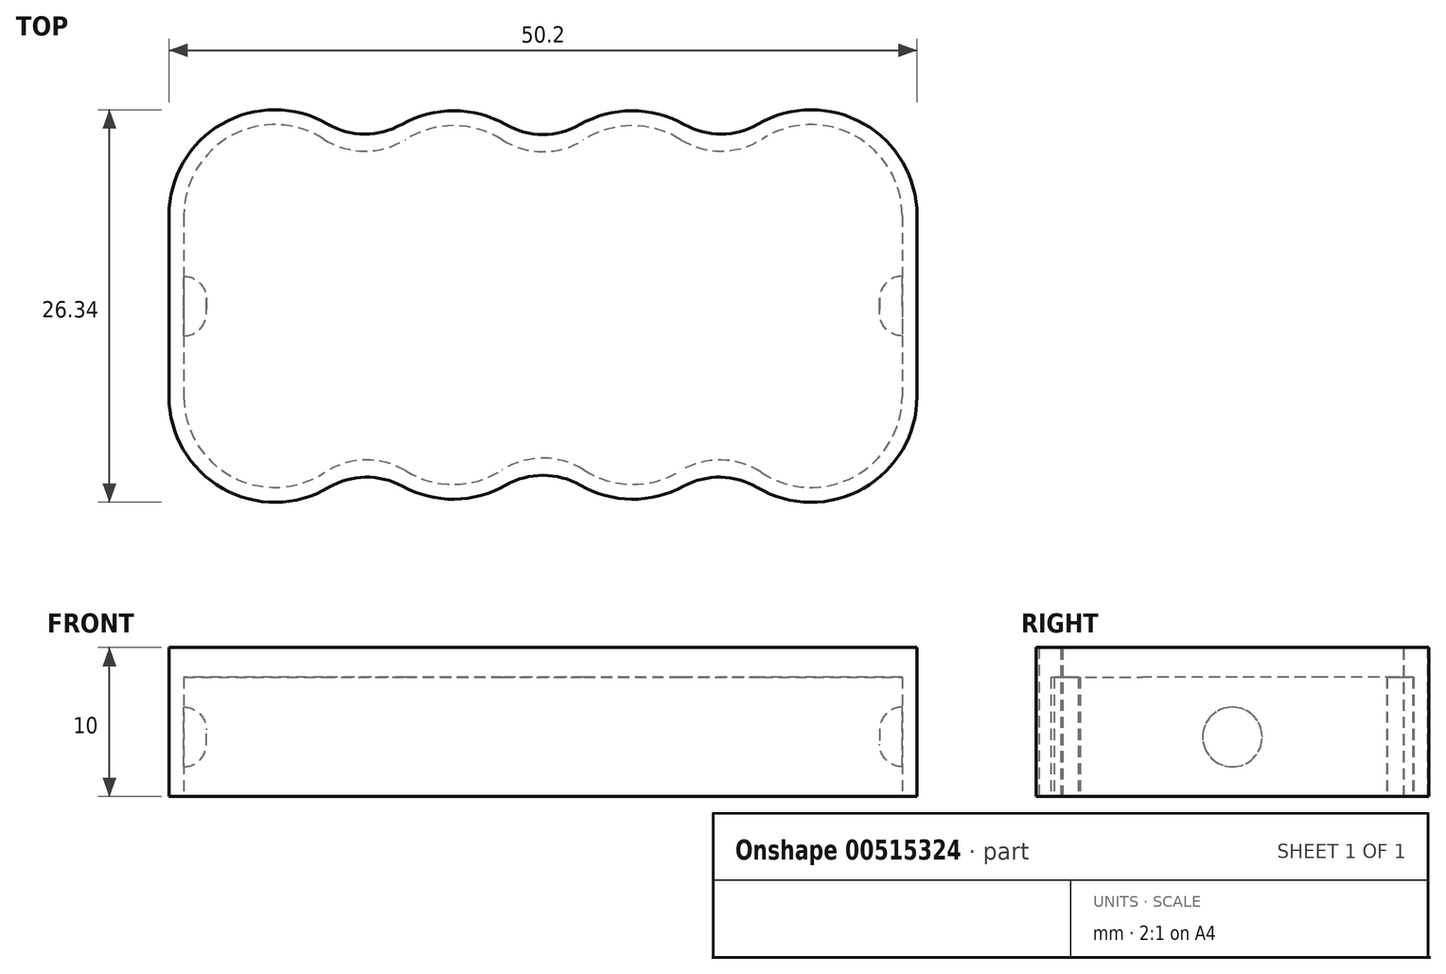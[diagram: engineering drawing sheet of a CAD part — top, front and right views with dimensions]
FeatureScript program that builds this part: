
annotation { "Feature Type Name" : "Feature", "Feature Type Description" : "" }
export const myFeature = defineFeature(function(context is Context, id is Id, definition is map)
    precondition{}
    {
        {
            var Q0;
            Q0=qCreatedBy(makeId("Top.planeOp"),FACE);
            var sketch = newSketch(context, id + "F0", { "sketchPlane" : qUnion([Q0])});
            skArc(sketch, "E0", {"start": v(-12, 7.13) * mm, "mid": v(-18.53, 12.15) * mm, "end": v(-24.1, 6.07) * mm});
            skArc(sketch, "E1", {"start": v(0, 7.1) * mm, "mid": v(-5.98, 12.1) * mm, "end": v(-12, 7.13) * mm});
            skArc(sketch, "E2.MirrorCS", {"start": v(0, -6.81) * mm, "mid": v(-5.86, -11.97) * mm, "end": v(-12, -7.13) * mm});
            skArc(sketch, "E3.MirrorCS", {"start": v(-12, -7.13) * mm, "mid": v(-18.53, -12.15) * mm, "end": v(-24.1, -6.07) * mm});
            skArc(sketch, "E4.MirrorCS", {"start": v(0, -6.81) * mm, "mid": v(5.86, -11.97) * mm, "end": v(12, -7.13) * mm});
            skArc(sketch, "E5.MirrorCS", {"start": v(12, 7.13) * mm, "mid": v(18.53, 12.15) * mm, "end": v(24.1, 6.07) * mm});
            skArc(sketch, "E6.MirrorCS", {"start": v(12, -7.13) * mm, "mid": v(18.53, -12.15) * mm, "end": v(24.1, -6.07) * mm});
            skArc(sketch, "E7.MirrorCS", {"start": v(0, 7.1) * mm, "mid": v(5.98, 12.1) * mm, "end": v(12, 7.13) * mm});
            skCircle(sketch, "E8", {"center": v(-12, 0) * mm, "radius": 2 * mm});
            skCircle(sketch, "E9", {"center": v(0, 0) * mm, "radius": 2 * mm});
            skCircle(sketch, "E10", {"center": v(12, 0) * mm, "radius": 2 * mm});
            skLineSegment(sketch, "E11", {"start": v(-24.1, 6.07) * mm, "end": v(-24.1, -6.07) * mm});
            skLineSegment(sketch, "E12", {"start": v(24.1, 6.07) * mm, "end": v(24.1, -6.07) * mm});
            skArc(sketch, "E13.0", {"start": v(-11.98, 9.83) * mm, "mid": v(-19.96, 12.9) * mm, "end": v(-25.1, 6.07) * mm});
            skArc(sketch, "E14.0", {"start": v(0, 9.8) * mm, "mid": v(-5.98, 13.1) * mm, "end": v(-11.98, 9.83) * mm});
            skArc(sketch, "E15.0", {"start": v(0, 9.8) * mm, "mid": v(5.98, 13.1) * mm, "end": v(11.98, 9.83) * mm});
            skArc(sketch, "E16.0", {"start": v(11.98, 9.83) * mm, "mid": v(19.96, 12.9) * mm, "end": v(25.1, 6.07) * mm});
            skLineSegment(sketch, "E17.0", {"start": v(25.1, 6.07) * mm, "end": v(25.1, -6.18) * mm});
            skArc(sketch, "E18.0", {"start": v(11.95, -9.78) * mm, "mid": v(19.93, -12.9) * mm, "end": v(25.1, -6.07) * mm});
            skArc(sketch, "E19.0", {"start": v(0, -9.62) * mm, "mid": v(5.93, -12.97) * mm, "end": v(11.95, -9.78) * mm});
            skArc(sketch, "E20.0", {"start": v(0, -9.62) * mm, "mid": v(-5.93, -12.97) * mm, "end": v(-11.95, -9.78) * mm});
            skArc(sketch, "E21.0", {"start": v(-11.95, -9.78) * mm, "mid": v(-19.93, -12.9) * mm, "end": v(-25.1, -6.07) * mm});
            skLineSegment(sketch, "E22.0", {"start": v(-25.1, 6.07) * mm, "end": v(-25.1, -6.18) * mm});
            skSolve(sketch);
        }
        {
            var Q0;
            Q0 = qSketchRegion(id + "F0", true);
            extrude(context, id + "F1", {"entities" : qUnion([Q0]), "depth" : 8 * mm, "offsetDistance" : 25 * mm});
        }
        {
            var Q0;
            Q0=makeQuery(id+"F1.opExtrude","SWEPT_EDGE",EDGE,{"disambiguationData":[OSD([sQuery(id+"F0.wireOp",EDGE,"E20.0"),sQuery(id+"F0.wireOp",EDGE,"E21.0")])]});
            var Q1;
            Q1=makeQuery(id+"F1.opExtrude","SWEPT_EDGE",EDGE,{"disambiguationData":[OSD([sQuery(id+"F0.wireOp",EDGE,"E19.0"),sQuery(id+"F0.wireOp",EDGE,"E20.0")])]});
            var Q2;
            Q2=makeQuery(id+"F1.opExtrude","SWEPT_EDGE",EDGE,{"disambiguationData":[OSD([sQuery(id+"F0.wireOp",EDGE,"E18.0"),sQuery(id+"F0.wireOp",EDGE,"E19.0")])]});
            var Q3;
            Q3=makeQuery(id+"F1.opExtrude","SWEPT_EDGE",EDGE,{"disambiguationData":[OSD([sQuery(id+"F0.wireOp",EDGE,"E13.0"),sQuery(id+"F0.wireOp",EDGE,"E14.0")])]});
            var Q4;
            Q4=makeQuery(id+"F1.opExtrude","SWEPT_EDGE",EDGE,{"disambiguationData":[OSD([sQuery(id+"F0.wireOp",EDGE,"E14.0"),sQuery(id+"F0.wireOp",EDGE,"E15.0")])]});
            var Q5;
            Q5=makeQuery(id+"F1.opExtrude","SWEPT_EDGE",EDGE,{"disambiguationData":[OSD([sQuery(id+"F0.wireOp",EDGE,"E15.0"),sQuery(id+"F0.wireOp",EDGE,"E16.0")])]});
            fillet(context, id + "F2", {"entities" : qUnion([Q0, Q1, Q2, Q3, Q4, Q5]), "radius" : 5 * mm, "tangentPropagation" : true, "allowEdgeOverflow" : false});
        }
        {
            var Q0;
            Q0=makeQuery(id+"F1.opExtrude","SWEPT_EDGE",EDGE,{"disambiguationData":[OSD([sQuery(id+"F0.wireOp",EDGE,"E2.MirrorCS"),sQuery(id+"F0.wireOp",EDGE,"E3.MirrorCS")])]});
            var Q1;
            Q1=makeQuery(id+"F1.opExtrude","SWEPT_EDGE",EDGE,{"disambiguationData":[OSD([sQuery(id+"F0.wireOp",EDGE,"E2.MirrorCS"),sQuery(id+"F0.wireOp",EDGE,"E4.MirrorCS")])]});
            var Q2;
            Q2=makeQuery(id+"F1.opExtrude","SWEPT_EDGE",EDGE,{"disambiguationData":[OSD([sQuery(id+"F0.wireOp",EDGE,"E4.MirrorCS"),sQuery(id+"F0.wireOp",EDGE,"E6.MirrorCS")])]});
            var Q3;
            Q3=makeQuery(id+"F1.opExtrude","SWEPT_EDGE",EDGE,{"disambiguationData":[OSD([sQuery(id+"F0.wireOp",EDGE,"E5.MirrorCS"),sQuery(id+"F0.wireOp",EDGE,"E7.MirrorCS")])]});
            var Q4;
            Q4=makeQuery(id+"F1.opExtrude","SWEPT_EDGE",EDGE,{"disambiguationData":[OSD([sQuery(id+"F0.wireOp",EDGE,"E1"),sQuery(id+"F0.wireOp",EDGE,"E7.MirrorCS")])]});
            var Q5;
            Q5=makeQuery(id+"F1.opExtrude","SWEPT_EDGE",EDGE,{"disambiguationData":[OSD([sQuery(id+"F0.wireOp",EDGE,"E0"),sQuery(id+"F0.wireOp",EDGE,"E1")])]});
            fillet(context, id + "F3", {"entities" : qUnion([Q0, Q1, Q2, Q3, Q4, Q5]), "radius" : 5.1 * mm, "tangentPropagation" : true, "allowEdgeOverflow" : false});
        }
        {
            var Q0;
            Q0=makeQuery(id+"F1.opExtrude","CAP_FACE",FACE,{"disambiguationData":[OSD([sQuery(id+"F0.wireOp",EDGE,"E0"),sQuery(id+"F0.wireOp",EDGE,"E1"),sQuery(id+"F0.wireOp",EDGE,"E2.MirrorCS"),sQuery(id+"F0.wireOp",EDGE,"E3.MirrorCS"),sQuery(id+"F0.wireOp",EDGE,"E4.MirrorCS"),sQuery(id+"F0.wireOp",EDGE,"E5.MirrorCS"),sQuery(id+"F0.wireOp",EDGE,"E6.MirrorCS"),sQuery(id+"F0.wireOp",EDGE,"E7.MirrorCS"),sQuery(id+"F0.wireOp",EDGE,"E11"),sQuery(id+"F0.wireOp",EDGE,"E12"),sQuery(id+"F0.wireOp",EDGE,"E13.0"),sQuery(id+"F0.wireOp",EDGE,"E14.0"),sQuery(id+"F0.wireOp",EDGE,"E15.0"),sQuery(id+"F0.wireOp",EDGE,"E16.0"),sQuery(id+"F0.wireOp",EDGE,"E17.0"),sQuery(id+"F0.wireOp",EDGE,"E18.0"),sQuery(id+"F0.wireOp",EDGE,"E19.0"),sQuery(id+"F0.wireOp",EDGE,"E20.0"),sQuery(id+"F0.wireOp",EDGE,"E21.0"),sQuery(id+"F0.wireOp",EDGE,"E22.0")])],"isStart":false});
            var sketch = newSketch(context, id + "F4", { "sketchPlane" : qUnion([Q0])});
            skArc(sketch, "E23", {"start": v(-14.44, 12.21) * mm, "mid": v(-21.55, 12.22) * mm, "end": v(-25.1, 6.07) * mm});
            skArc(sketch, "E24", {"start": v(-14.44, 12.21) * mm, "mid": v(-11.97, 11.54) * mm, "end": v(-9.48, 12.19) * mm});
            skArc(sketch, "E25", {"start": v(-2.48, 12.17) * mm, "mid": v(-5.98, 13.1) * mm, "end": v(-9.48, 12.19) * mm});
            skArc(sketch, "E26", {"start": v(-2.48, 12.17) * mm, "mid": v(0, 11.5) * mm, "end": v(2.48, 12.17) * mm});
            skArc(sketch, "E27", {"start": v(9.48, 12.19) * mm, "mid": v(5.98, 13.1) * mm, "end": v(2.48, 12.17) * mm});
            skArc(sketch, "E28", {"start": v(9.48, 12.19) * mm, "mid": v(11.97, 11.54) * mm, "end": v(14.44, 12.21) * mm});
            skArc(sketch, "E29", {"start": v(25.1, 6.07) * mm, "mid": v(21.55, 12.22) * mm, "end": v(14.44, 12.21) * mm});
            skArc(sketch, "E30", {"start": v(14.38, -12.18) * mm, "mid": v(21.52, -12.24) * mm, "end": v(25.1, -6.07) * mm});
            skArc(sketch, "E31", {"start": v(14.38, -12.18) * mm, "mid": v(11.92, -11.48) * mm, "end": v(9.44, -12.1) * mm});
            skArc(sketch, "E32", {"start": v(2.5, -12.02) * mm, "mid": v(5.95, -12.97) * mm, "end": v(9.44, -12.1) * mm});
            skArc(sketch, "E33", {"start": v(2.5, -12.02) * mm, "mid": v(0, -11.36) * mm, "end": v(-2.5, -12.02) * mm});
            skArc(sketch, "E34", {"start": v(-9.44, -12.1) * mm, "mid": v(-5.95, -12.97) * mm, "end": v(-2.5, -12.02) * mm});
            skArc(sketch, "E35", {"start": v(-9.44, -12.1) * mm, "mid": v(-11.92, -11.48) * mm, "end": v(-14.38, -12.18) * mm});
            skArc(sketch, "E36", {"start": v(-25.1, -6.07) * mm, "mid": v(-21.52, -12.24) * mm, "end": v(-14.38, -12.18) * mm});
            skLineSegment(sketch, "E37", {"start": v(-25.1, 6.07) * mm, "end": v(-25.1, -6.07) * mm});
            skLineSegment(sketch, "E38", {"start": v(25.1, 6.07) * mm, "end": v(25.1, -6.07) * mm});
            skSolve(sketch);
        }
        {
            var Q0;
            Q0 = qSketchRegion(id + "F4", true);
            extrude(context, id + "F5", {"entities" : qUnion([Q0]), "operationType" : NewBodyOperationType.ADD, "depth" : 2 * mm, "offsetDistance" : 25 * mm});
        }
        {
            var Q0;
            Q0=makeQuery(id+"F1.opExtrude","SWEPT_FACE",FACE,{"disambiguationData":[OSD([sQuery(id+"F0.wireOp",EDGE,"E11")])]});
            var sketch = newSketch(context, id + "F6", { "sketchPlane" : qUnion([Q0])});
            skCircle(sketch, "E39", {"center": v(0, 4) * mm, "radius": 2 * mm});
            skSolve(sketch);
        }
        {
            var Q0;
            Q0 = qSketchRegion(id + "F6", true);
            extrude(context, id + "F7", {"entities" : qUnion([Q0]), "operationType" : NewBodyOperationType.ADD, "depth" : 1.5 * mm, "offsetDistance" : 25 * mm});
        }
        {
            var Q0;
            Q0=makeQuery(id+"F7.opExtrude","CAP_FACE",FACE,{"disambiguationData":[OSD([sQuery(id+"F6.wireOp",EDGE,"E39")])],"isStart":false});
            fillet(context, id + "F8", {"entities" : qUnion([Q0]), "radius" : 1.5 * mm, "tangentPropagation" : true, "allowEdgeOverflow" : false});
        }
        {
            var Q0;
            Q0=makeQuery(id+"F1.opExtrude","SWEPT_FACE",FACE,{"disambiguationData":[OSD([sQuery(id+"F0.wireOp",EDGE,"E12")])]});
            var sketch = newSketch(context, id + "F9", { "sketchPlane" : qUnion([Q0])});
            skCircle(sketch, "E40", {"center": v(0, 4) * mm, "radius": 2 * mm});
            skSolve(sketch);
        }
        {
            var Q0;
            Q0 = qSketchRegion(id + "F9", true);
            extrude(context, id + "F10", {"entities" : qUnion([Q0]), "operationType" : NewBodyOperationType.ADD, "depth" : 1.5 * mm, "offsetDistance" : 25 * mm});
        }
        {
            var Q0;
            Q0=makeQuery(id+"F10.opExtrude","CAP_FACE",FACE,{"disambiguationData":[OSD([sQuery(id+"F9.wireOp",EDGE,"E40")])],"isStart":false});
            fillet(context, id + "F11", {"entities" : qUnion([Q0]), "radius" : 1.5 * mm, "tangentPropagation" : true, "allowEdgeOverflow" : false});
        }
    });
